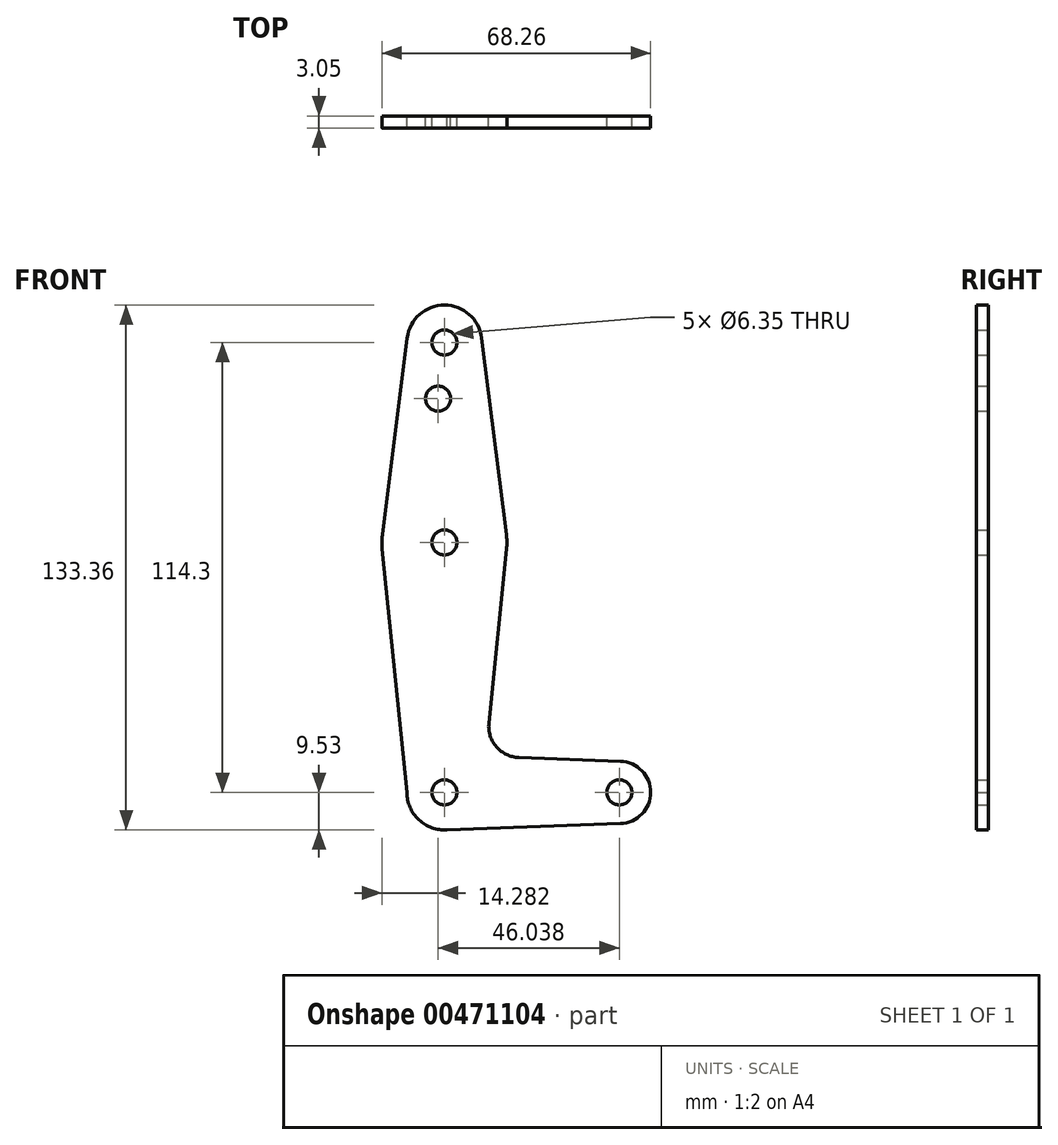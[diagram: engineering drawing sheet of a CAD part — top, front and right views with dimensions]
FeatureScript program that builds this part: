
annotation { "Feature Type Name" : "Feature", "Feature Type Description" : "" }
export const myFeature = defineFeature(function(context is Context, id is Id, definition is map)
    precondition{}
    {
        {
            var Q0;
            Q0=qCreatedBy(makeId("Front.planeOp"),FACE);
            var sketch = newSketch(context, id + "F0", { "sketchPlane" : qUnion([Q0])});
            skLineSegment(sketch, "E0", {"start": v(0, 0) * mm, "end": v(44.45, 0) * mm, "construction": true});
            skLineSegment(sketch, "E1", {"start": v(0, 0) * mm, "end": v(0, 114.3) * mm, "construction": true});
            skCircle(sketch, "E2", {"center": v(0, 114.3) * mm, "radius": 9.53 * mm});
            skCircle(sketch, "E3", {"center": v(44.45, 0) * mm, "radius": 7.94 * mm});
            skCircle(sketch, "E4", {"center": v(0, 63.5) * mm, "radius": 15.88 * mm});
            skCircle(sketch, "E5", {"center": v(0, 0) * mm, "radius": 9.53 * mm});
            skLineSegment(sketch, "E6", {"start": v(15.75, 65.48) * mm, "end": v(9.45, 115.5) * mm});
            skLineSegment(sketch, "E7", {"start": v(18.93, 8.85) * mm, "end": v(44.73, 7.93) * mm});
            skLineSegment(sketch, "E8", {"start": v(0, -9.53) * mm, "end": v(44.73, -7.93) * mm});
            skLineSegment(sketch, "E9", {"start": v(-9.45, 115.5) * mm, "end": v(-15.75, 65.48) * mm});
            skLineSegment(sketch, "E10", {"start": v(-9.53, 0) * mm, "end": v(-15.8, 61.9) * mm});
            skLineSegment(sketch, "E11", {"start": v(11.3, 17.6) * mm, "end": v(15.8, 61.9) * mm});
            skPoint(sketch, "E11.startSnap0", {"position": v(22.23, 0) * mm});
            skPoint(sketch, "E12.newPointA", {"position": v(9.53, 0) * mm});
            skPoint(sketch, "E12.newPointB", {"position": v(0, 9.53) * mm});
            skArc(sketch, "E12.filletArc", {"start": v(11.3, 17.6) * mm, "mid": v(13.22, 11.57) * mm, "end": v(18.93, 8.85) * mm});
            skCircle(sketch, "E13", {"center": v(0, 114.3) * mm, "radius": 3.18 * mm});
            skCircle(sketch, "E14", {"center": v(0, 63.5) * mm, "radius": 3.18 * mm});
            skCircle(sketch, "E15", {"center": v(-1.59, 100.03) * mm, "radius": 3.18 * mm});
            skCircle(sketch, "E16", {"center": v(0, 0) * mm, "radius": 3.18 * mm});
            skCircle(sketch, "E17", {"center": v(44.45, 0) * mm, "radius": 3.18 * mm});
            skSolve(sketch);
        }
        {
            var Q0;
            Q0 = qSketchRegion(id + "F0", true);
            extrude(context, id + "F1", {"entities" : qUnion([Q0]), "depth" : 3.05 * mm});
        }
    });
